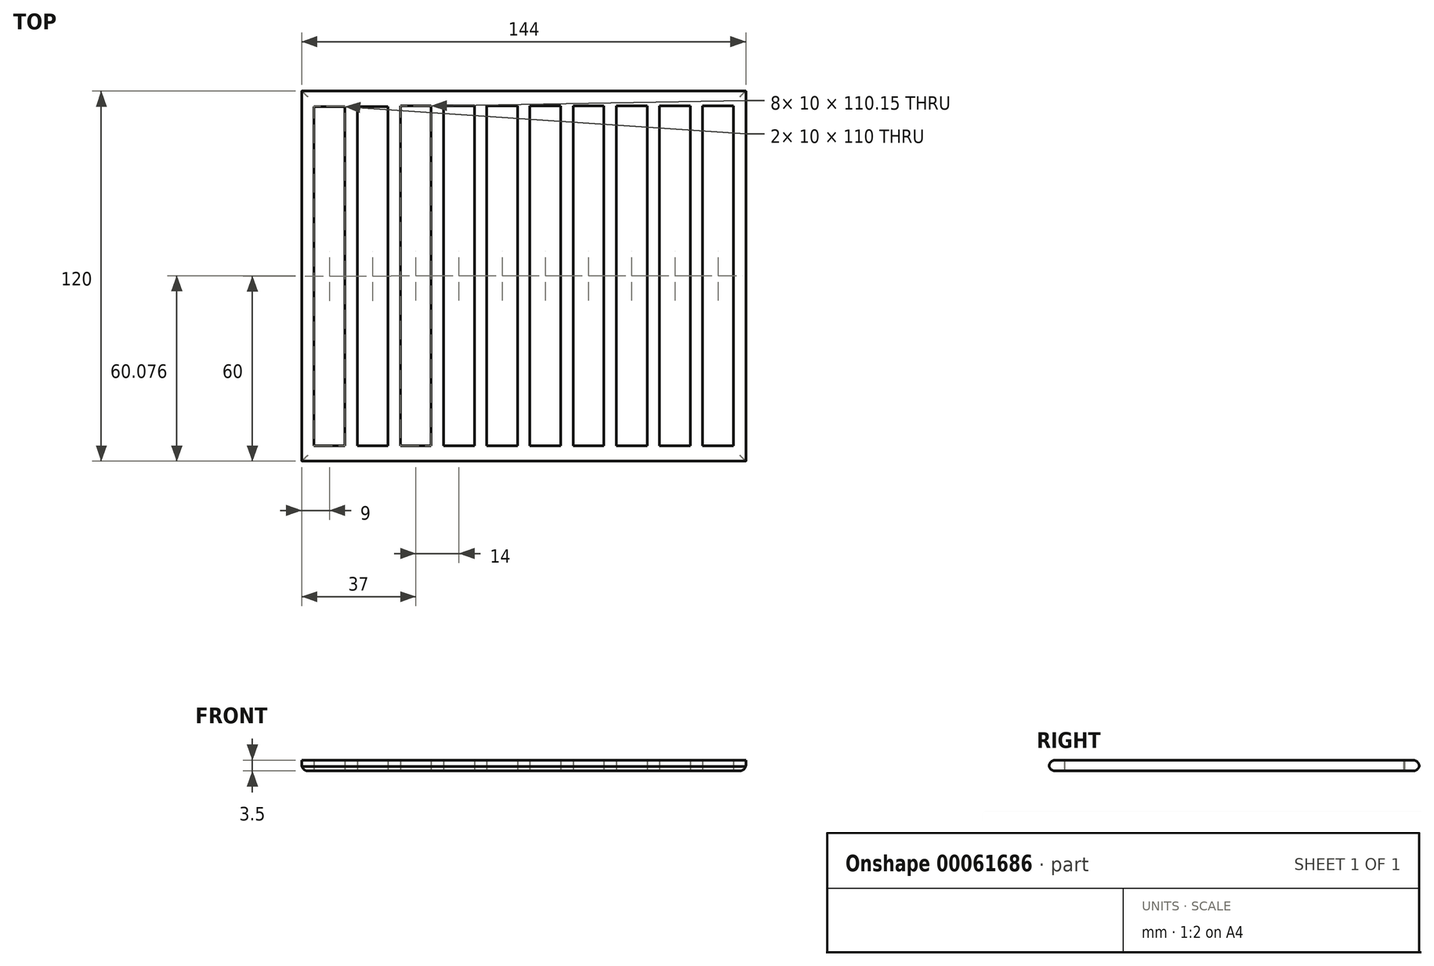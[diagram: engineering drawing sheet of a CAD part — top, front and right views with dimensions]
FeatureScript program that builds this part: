
annotation { "Feature Type Name" : "Feature", "Feature Type Description" : "" }
export const myFeature = defineFeature(function(context is Context, id is Id, definition is map)
    precondition{}
    {
        {
            var Q0;
            Q0=qCreatedBy(makeId("Top.planeOp"),FACE);
            var sketch = newSketch(context, id + "F0", { "sketchPlane" : qUnion([Q0])});
            skLineSegment(sketch, "E0.rect.bottom", {"start": v(-72, 60) * mm, "end": v(72, 60) * mm});
            skLineSegment(sketch, "E0.rect.top", {"start": v(-72, -60) * mm, "end": v(72, -60) * mm});
            skLineSegment(sketch, "E0.rect.left", {"start": v(-72, 60) * mm, "end": v(-72, -60) * mm});
            skLineSegment(sketch, "E0.rect.right", {"start": v(72, 60) * mm, "end": v(72, -60) * mm});
            skPoint(sketch, "E0.rect.middle", {"position": v(0, 0) * mm});
            skLineSegment(sketch, "E1.bottom", {"start": v(-68, 55) * mm, "end": v(-58, 55) * mm});
            skLineSegment(sketch, "E1.top", {"start": v(-68, -55) * mm, "end": v(-58, -55) * mm});
            skLineSegment(sketch, "E1.left", {"start": v(-68, 55) * mm, "end": v(-68, -55) * mm});
            skLineSegment(sketch, "E1.right", {"start": v(-58, 55) * mm, "end": v(-58, -55) * mm});
            skLineSegment(sketch, "E2.bottom", {"start": v(-54, 55) * mm, "end": v(-44, 55) * mm});
            skLineSegment(sketch, "E2.right", {"start": v(-44, 55) * mm, "end": v(-44, -55) * mm});
            skLineSegment(sketch, "E2.left", {"start": v(-54, 55) * mm, "end": v(-54, -55) * mm});
            skLineSegment(sketch, "E2.top", {"start": v(-54, -55) * mm, "end": v(-44, -55) * mm});
            skLineSegment(sketch, "E3.bottom", {"start": v(-26, 55.15) * mm, "end": v(-16, 55.15) * mm});
            skLineSegment(sketch, "E3.left", {"start": v(-26, 55.15) * mm, "end": v(-26, -55) * mm});
            skLineSegment(sketch, "E3.right", {"start": v(-16, 55.15) * mm, "end": v(-16, -55) * mm});
            skLineSegment(sketch, "E3.top", {"start": v(-26, -55) * mm, "end": v(-16, -55) * mm});
            skLineSegment(sketch, "E4.top", {"start": v(-40, -55) * mm, "end": v(-30, -55) * mm});
            skLineSegment(sketch, "E4.right", {"start": v(-30, 55.15) * mm, "end": v(-30, -55) * mm});
            skLineSegment(sketch, "E4.left", {"start": v(-40, 55.15) * mm, "end": v(-40, -55) * mm});
            skLineSegment(sketch, "E4.bottom", {"start": v(-40, 55.15) * mm, "end": v(-30, 55.15) * mm});
            skLineSegment(sketch, "E5.bottom", {"start": v(-12, 55.15) * mm, "end": v(-2, 55.15) * mm});
            skLineSegment(sketch, "E5.right", {"start": v(-2, 55.15) * mm, "end": v(-2, -55) * mm});
            skLineSegment(sketch, "E5.left", {"start": v(-12, 55.15) * mm, "end": v(-12, -55) * mm});
            skLineSegment(sketch, "E5.top", {"start": v(-12, -55) * mm, "end": v(-2, -55) * mm});
            skLineSegment(sketch, "E6.top", {"start": v(2, -55) * mm, "end": v(12, -55) * mm});
            skLineSegment(sketch, "E6.right", {"start": v(12, 55.15) * mm, "end": v(12, -55) * mm});
            skLineSegment(sketch, "E6.left", {"start": v(2, 55.15) * mm, "end": v(2, -55) * mm});
            skLineSegment(sketch, "E6.bottom", {"start": v(2, 55.15) * mm, "end": v(12, 55.15) * mm});
            skLineSegment(sketch, "E7.bottom", {"start": v(16, 55.15) * mm, "end": v(26, 55.15) * mm});
            skLineSegment(sketch, "E7.left", {"start": v(16, 55.15) * mm, "end": v(16, -55) * mm});
            skLineSegment(sketch, "E7.right", {"start": v(26, 55.15) * mm, "end": v(26, -55) * mm});
            skLineSegment(sketch, "E7.top", {"start": v(16, -55) * mm, "end": v(26, -55) * mm});
            skLineSegment(sketch, "E8.top", {"start": v(30, -55) * mm, "end": v(40, -55) * mm});
            skLineSegment(sketch, "E8.right", {"start": v(40, 55.15) * mm, "end": v(40, -55) * mm});
            skLineSegment(sketch, "E8.left", {"start": v(30, 55.15) * mm, "end": v(30, -55) * mm});
            skLineSegment(sketch, "E8.bottom", {"start": v(30, 55.15) * mm, "end": v(40, 55.15) * mm});
            skLineSegment(sketch, "E9.bottom", {"start": v(44, 55.15) * mm, "end": v(54, 55.15) * mm});
            skLineSegment(sketch, "E10.top", {"start": v(58, -55) * mm, "end": v(68, -55) * mm});
            skLineSegment(sketch, "E9.top", {"start": v(44, -55) * mm, "end": v(54, -55) * mm});
            skLineSegment(sketch, "E9.left", {"start": v(44, 55.15) * mm, "end": v(44, -55) * mm});
            skLineSegment(sketch, "E9.right", {"start": v(54, 55.15) * mm, "end": v(54, -55) * mm});
            skLineSegment(sketch, "E10.right", {"start": v(68, 55.15) * mm, "end": v(68, -55) * mm});
            skLineSegment(sketch, "E10.left", {"start": v(58, 55.15) * mm, "end": v(58, -55) * mm});
            skLineSegment(sketch, "E10.bottom", {"start": v(58, 55.15) * mm, "end": v(68, 55.15) * mm});
            skSolve(sketch);
        }
        {
            var Q0;
            Q0=makeQuery(id+"F0.imprint","IMPRINT",FACE,{"disambiguationData":[TD([[makeQuery(id+"F0.imprint","IMPRINT",EDGE,{"derivedFrom":sQuery(id+"F0.wireOp",EDGE,"E0.rect.bottom")}),-1.0]])]});
            extrude(context, id + "F1", {"entities" : qUnion([Q0]), "depth" : 3.5 * mm});
        }
        {
            var Q0;
            Q0=makeQuery(id+"F1.opExtrude","CAP_EDGE",EDGE,{"disambiguationData":[OSD([sQuery(id+"F0.wireOp",EDGE,"E0.rect.bottom")])],"isStart":false});
            var Q1;
            Q1=makeQuery(id+"F1.opExtrude","CAP_EDGE",EDGE,{"disambiguationData":[OSD([sQuery(id+"F0.wireOp",EDGE,"E0.rect.top")])],"isStart":false});
            fillet(context, id + "F2", {"entities" : qUnion([Q0, Q1]), "radius" : 2 * mm, "tangentPropagation" : true, "allowEdgeOverflow" : false});
        }
        {
            var Q0;
            Q0=makeQuery(id+"F1.opExtrude","CAP_EDGE",EDGE,{"disambiguationData":[OSD([sQuery(id+"F0.wireOp",EDGE,"E0.rect.top")])],"isStart":true});
            var Q1;
            Q1=makeQuery(id+"F1.opExtrude","CAP_EDGE",EDGE,{"disambiguationData":[OSD([sQuery(id+"F0.wireOp",EDGE,"E0.rect.bottom")])],"isStart":true});
            fillet(context, id + "F3", {"entities" : qUnion([Q0, Q1]), "radius" : 2 * mm, "tangentPropagation" : true, "allowEdgeOverflow" : false});
        }
        {
            var Q0;
            Q0=makeQuery(id+"F1.opExtrude","CAP_EDGE",EDGE,{"disambiguationData":[OSD([sQuery(id+"F0.wireOp",EDGE,"E0.rect.left")])],"isStart":true});
            var Q1;
            Q1=makeQuery(id+"F1.opExtrude","CAP_EDGE",EDGE,{"disambiguationData":[OSD([sQuery(id+"F0.wireOp",EDGE,"E0.rect.right")])],"isStart":true});
            fillet(context, id + "F4", {"entities" : qUnion([Q0, Q1]), "radius" : 2 * mm, "tangentPropagation" : true, "allowEdgeOverflow" : false});
        }
    });
